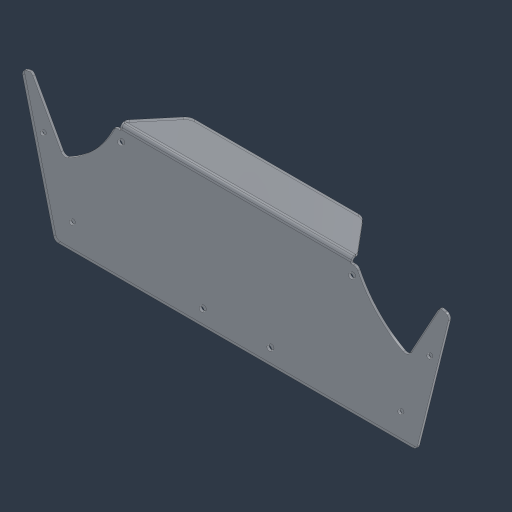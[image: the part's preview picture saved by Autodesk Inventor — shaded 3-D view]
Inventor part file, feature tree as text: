
AUTODESK INVENTOR PART (.ipt)
format: ipt  version: 2024.3 (Build 283343000, 343)  size: 292,864 bytes
history: native  units: in
note: dims shown in document units (in); Inventor stores cm internally (conversion verified against a paired STEP export)
features: sketch x7, other x5, sheet_metal_op x4, chamfer x3, hole x3, projected_geometry x1
ambient origin geometry x8: Origin, YZ Plane, XZ Plane, XY Plane, X Axis, Y Axis, Z Axis, Center Point
bodies: Solid1 (feature_tree)
feature tree (23):
  sheet_metal_op  "Face1"
  chamfer  "Corner Round1"
  hole  "Hole1"  [1 undecoded]
  chamfer  "Corner Round2"
  hole  "Hole2"  [1 undecoded]
  sheet_metal_op  "Flange2"
  chamfer  "Corner Round4"
  hole  "Hole3"  [1 undecoded]
  sketch  "Sketch1"  dims[d0=2.75in d1=5.0in]
  other  "Plate1"
  sketch  "Sketch6"  dims[d2=7.5in d3=0.12in]
  sketch  "Sketch7"  dims[d4=0.25in d19=0.25in]
  projected_geometry  "Projected Loop3"
  sketch  "Sketch9"  dims[d22=4.5in]
  sketch  "Sketch10"  dims[d23=10.0in]
  other  "Plate3"
  sheet_metal_op  "Bend2"
  sheet_metal_op  "Corner2"
  sketch  "Sketch11"  dims[d24=10.0in]
  sketch  "Sketch12"  dims[d25=0.201in d26=0.75in d27=0.385in d28=0.25in d29=0.5635in d30=0.12in d31=0.8108in d32=5.5in d33=3.0in d34=4.5in d35=1.0in d36=0.12in d37=0.0in d38=0.25in d39=8.5in d40=8.5in d41=1.25in d42=1.25in d43=1.75in d44=1.75in d45=0.75in d46=0.75in d47=0.25in d48=0.75in d49=0.385in d50=0.25in d51=0.5635in d52=0.12in d53=0.8108in d54=0.12in d55=0.06in d56=0.24in d57=0.12in d58=2.125in d59=90.0deg d60=0.12in d61=0.48in d62=0.12in d63=0.12in d67=0.12in d68=0.0in d70=0.8933in d71=1.5in d72=0.25in d73=1.5in d74=0.3436in d75=0.5in d76=0.5625in d79=0.25in d80=0.75in d81=0.375in d82=0.25in d83=0.5635in d84=0.12in d85=0.8108in]
  other  "Cut3"
  other  "Cut4"
  other  "Definition1"
note: 3 required parameter values undecoded (feature->parameter linkage not recoverable at this tier; creation-order binding heuristic only, values carry confidence <= 0.55)
